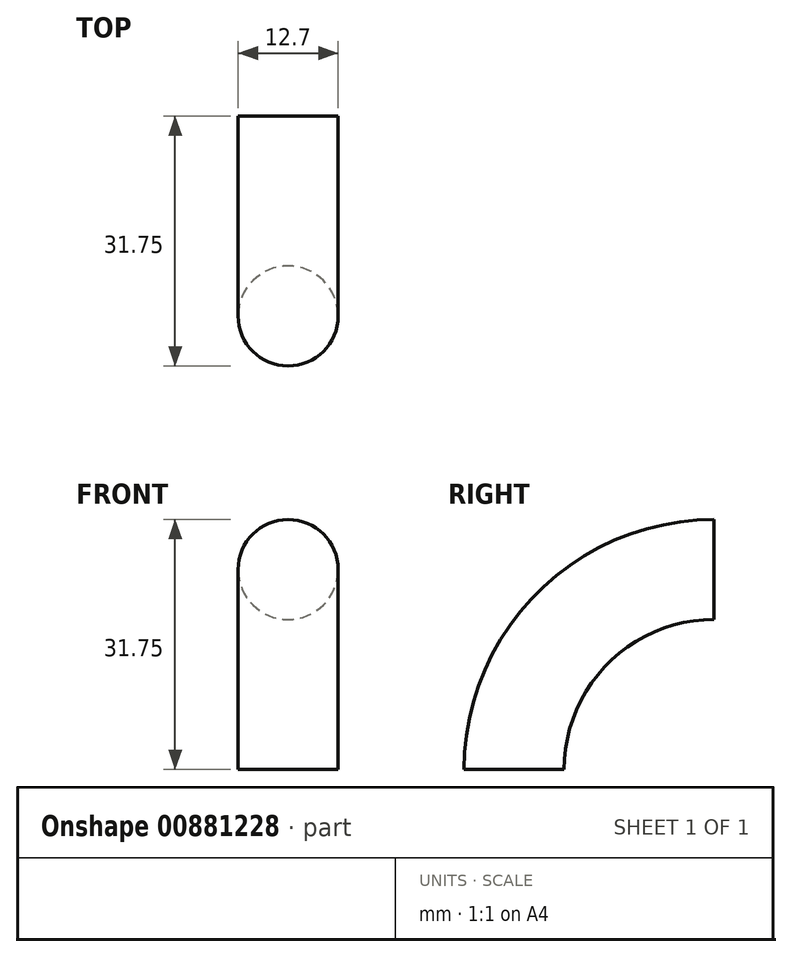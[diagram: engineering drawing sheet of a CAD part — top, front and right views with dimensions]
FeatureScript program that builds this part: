
annotation { "Feature Type Name" : "Feature", "Feature Type Description" : "" }
export const myFeature = defineFeature(function(context is Context, id is Id, definition is map)
    precondition{}
    {
        {
            var Q0;
            Q0=qCreatedBy(makeId("Top.planeOp"),FACE);
            var sketch = newSketch(context, id + "F0", { "sketchPlane" : qUnion([Q0])});
            skCircle(sketch, "E0", {"center": v(0, 0) * mm, "radius": 6.35 * mm});
            skSolve(sketch);
        }
        {
            var Q0;
            Q0=qCreatedBy(makeId("Right.planeOp"),FACE);
            var sketch = newSketch(context, id + "F1", { "sketchPlane" : qUnion([Q0])});
            skArc(sketch, "E1", {"start": v(25.4, 25.4) * mm, "mid": v(7.44, 17.96) * mm, "end": v(0, 0) * mm});
            skSolve(sketch);
        }
        {
            var Q0;
            Q0=makeQuery(id+"F0.imprint","IMPRINT",FACE,{"disambiguationData":[TD([[makeQuery(id+"F0.imprint","IMPRINT",EDGE,{"derivedFrom":sQuery(id+"F0.wireOp",EDGE,"E0")}),1.0]])]});
            var Q1;
            Q1=sQuery(id+"F0.wireOp",EDGE,"E0");
            var Q2;
            Q2=sQuery(id+"F1.wireOp",EDGE,"E1");
            sweep(context, id + "F2", {"bodyType" : ToolBodyType.SURFACE, "profiles" : qUnion([Q0]), "surfaceProfiles" : qUnion([Q1]), "path" : qUnion([Q2])});
        }
    });
